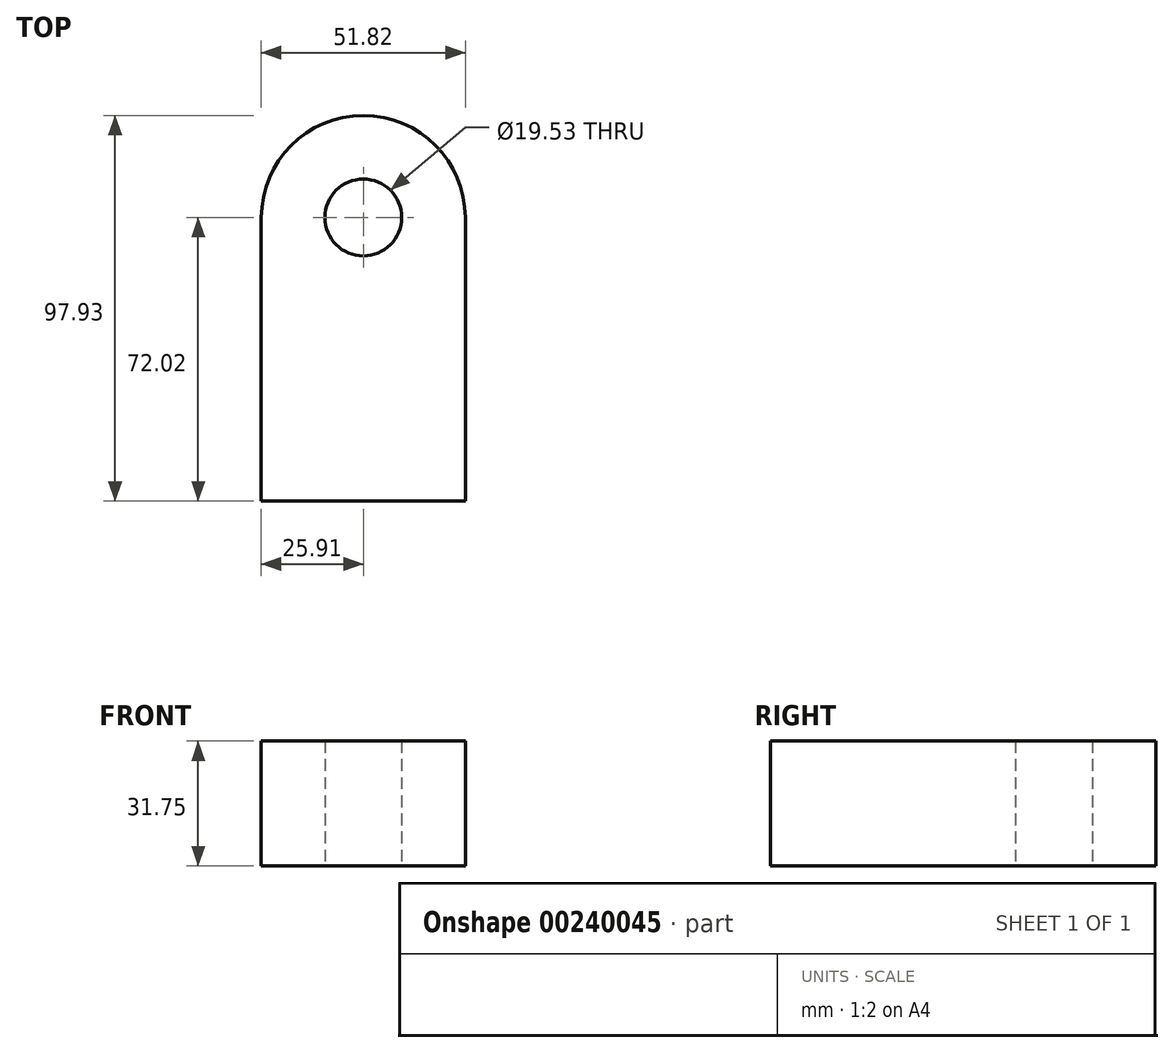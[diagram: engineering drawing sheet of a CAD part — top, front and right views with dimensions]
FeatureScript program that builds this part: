
annotation { "Feature Type Name" : "Feature", "Feature Type Description" : "" }
export const myFeature = defineFeature(function(context is Context, id is Id, definition is map)
    precondition{}
    {
        {
            var Q0;
            Q0=qCreatedBy(makeId("Top.planeOp"),FACE);
            var sketch = newSketch(context, id + "F0", { "sketchPlane" : qUnion([Q0])});
            skLineSegment(sketch, "E0.bottom", {"start": v(25.9, -36) * mm, "end": v(-25.9, -36) * mm});
            skLineSegment(sketch, "E0.left", {"start": v(25.9, -36) * mm, "end": v(25.9, 36) * mm});
            skLineSegment(sketch, "E0.right", {"start": v(-25.9, -36) * mm, "end": v(-25.9, 36) * mm});
            skPoint(sketch, "E0.middle", {"position": v(0, 0) * mm});
            skArc(sketch, "E1", {"start": v(25.9, 36) * mm, "mid": v(0, 61.92) * mm, "end": v(-25.9, 36) * mm});
            skCircle(sketch, "E2", {"center": v(0, 36) * mm, "radius": 9.77 * mm});
            skSolve(sketch);
        }
        {
            var Q0;
            Q0=makeQuery(id+"F0.imprint","IMPRINT",FACE,{"disambiguationData":[TD([[makeQuery(id+"F0.imprint","IMPRINT",EDGE,{"derivedFrom":sQuery(id+"F0.wireOp",EDGE,"E0.bottom")}),-1.0]])]});
            extrude(context, id + "F1", {"entities" : qUnion([Q0]), "depth" : 31.75 * mm});
        }
    });
